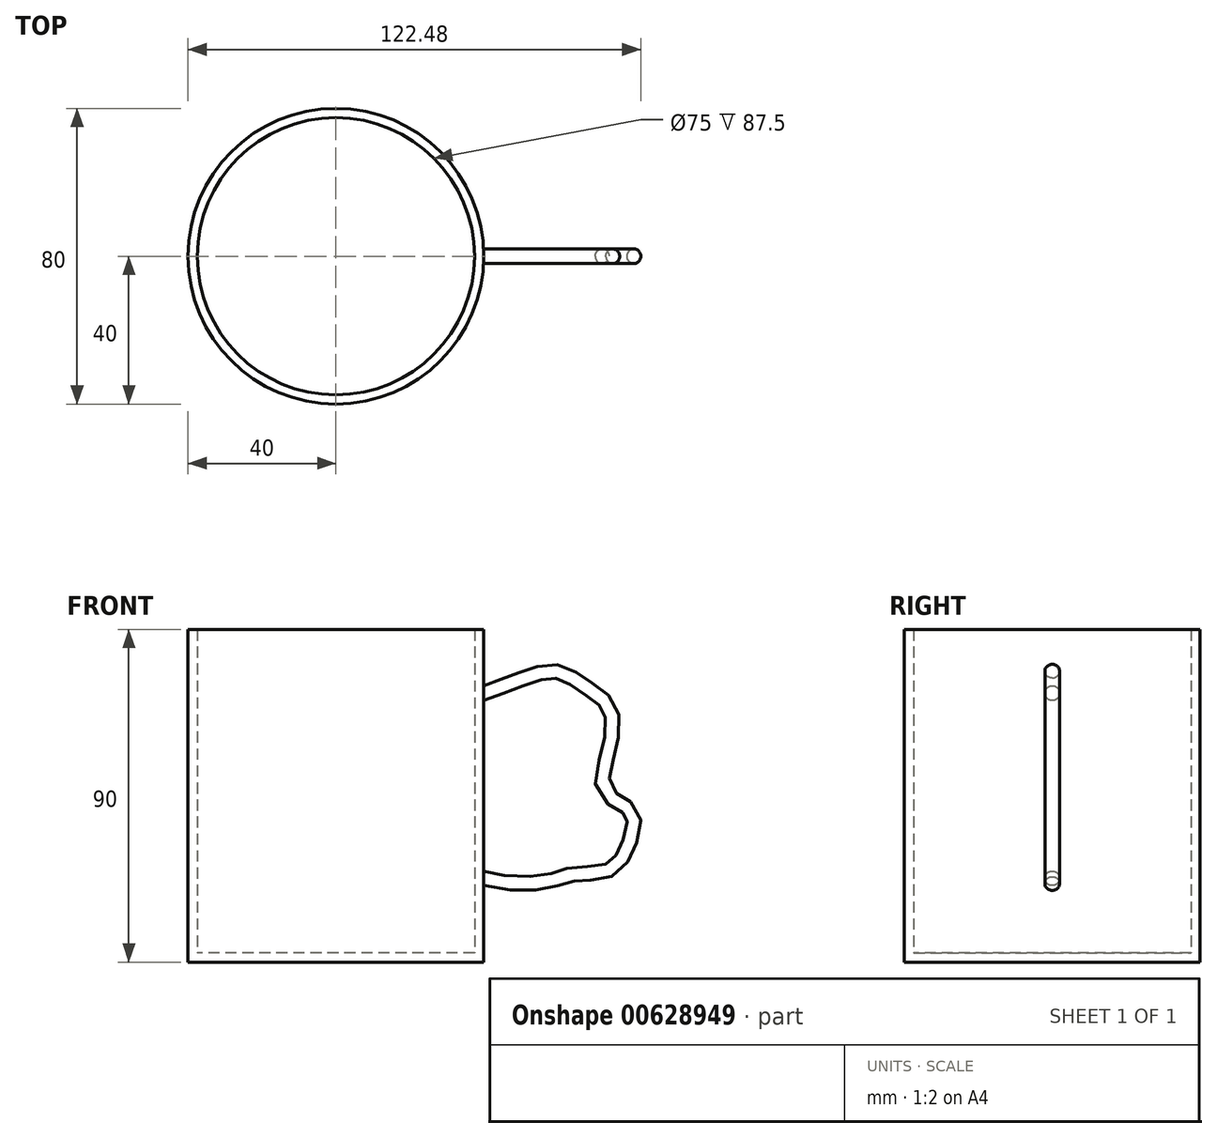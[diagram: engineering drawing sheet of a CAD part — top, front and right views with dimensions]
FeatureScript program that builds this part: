
annotation { "Feature Type Name" : "Feature", "Feature Type Description" : "" }
export const myFeature = defineFeature(function(context is Context, id is Id, definition is map)
    precondition{}
    {
        {
            var Q0;
            Q0=qCreatedBy(makeId("Top.planeOp"),FACE);
            var sketch = newSketch(context, id + "F0", { "sketchPlane" : qUnion([Q0])});
            skCircle(sketch, "E0", {"center": v(0, 0) * mm, "radius": 40 * mm});
            skSolve(sketch);
        }
        {
            var Q0;
            Q0=makeQuery(id+"F0.imprint","IMPRINT",FACE,{"disambiguationData":[TD([[makeQuery(id+"F0.imprint","IMPRINT",EDGE,{"derivedFrom":sQuery(id+"F0.wireOp",EDGE,"E0")}),1.0]])]});
            var Q1;
            Q1 = qSketchRegion(id + "F0", true);
            extrude(context, id + "F1", {"entities" : qUnion([Q0, Q1]), "depth" : 90 * mm, "offsetDistance" : 25 * mm});
        }
        {
            var Q0;
            Q0=qCreatedBy(makeId("Front.planeOp"),FACE);
            var sketch = newSketch(context, id + "F2", { "sketchPlane" : qUnion([Q0])});
            skFitSpline(sketch, "E1", {"points": [v(39.51, 73.13) * mm, v(50.1, 77.1) * mm, v(60, 79.08) * mm, v(67.94, 74.78) * mm, v(74.56, 68.83) * mm, v(74.23, 56.93) * mm, v(73.23, 46.35) * mm, v(80.18, 41.06) * mm, v(79.85, 32.13) * mm, v(74.23, 24.53) * mm, v(63.98, 23.2) * mm, v(56.7, 21.22) * mm, v(39.84, 22.21) * mm, v(33.23, 26.51) * mm], "startDerivative": vector(128.25, 48.64) * mm, "endDerivative": vector(-75.92, 71.45) * mm});
            skSolve(sketch);
        }
        {
            var Q0;
            Q0=qCreatedBy(makeId("Right.planeOp"),FACE);
            cPlane(context, id + "F3", {"entities" : qUnion([Q0]), "cplaneType" : CPlaneType.OFFSET, "offset" : 40 * mm, "width" : 150 * mm, "height" : 150 * mm});
        }
        {
            var Q0;
            Q0=qCreatedBy(id+"F3.planeOp",FACE);
            var sketch = newSketch(context, id + "F4", { "sketchPlane" : qUnion([Q0])});
            skCircle(sketch, "E2", {"center": v(0, 72.78) * mm, "radius": 2 * mm});
            skSolve(sketch);
        }
        {
            var Q0;
            Q0 = qSketchRegion(id + "F4", true);
            var Q1;
            Q1=sQuery(id+"F2.wireOp",EDGE,"E1");
            sweep(context, id + "F5", {"operationType" : NewBodyOperationType.ADD, "profiles" : qUnion([Q0]), "path" : qUnion([Q1])});
        }
        {
            var Q0;
            Q0=makeQuery(id+"F1.opExtrude","CAP_FACE",FACE,{"disambiguationData":[OSD([sQuery(id+"F0.wireOp",EDGE,"E0")])],"isStart":false});
            shell(context, id + "F6", {"entities" : qUnion([Q0]), "thickness" : 2.5 * mm});
        }
    });
